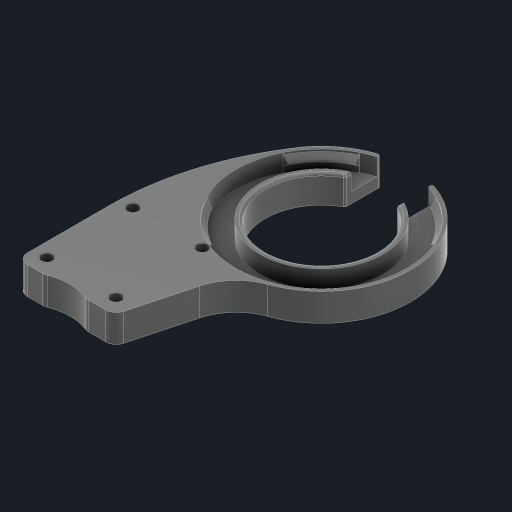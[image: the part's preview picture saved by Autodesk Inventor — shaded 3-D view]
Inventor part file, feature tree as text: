
AUTODESK INVENTOR PART (.ipt)
format: ipt  version: 2023 (Build 270158000, 158)  size: 347,136 bytes
history: native  units: mm
features: extrude x8, fillet x7, sketch x5, draft x2, revolve x1, direct_edit x1, other x1
ambient origin geometry x8: Origin, YZ Plane, XZ Plane, XY Plane, X Axis, Y Axis, Z Axis, Center Point
bodies: Solid1 (feature_tree)
feature tree (25):
  sketch  "Sketch1"  dims[d0=35.5mm d2=49.02mm]
  extrude  "Extrusion1"  Depth=49.02mm
  extrude  "Extrusion2"  Depth=7.0mm TaperAngle=0.0deg
  draft  "FaceDraft1"
  sketch  "Sketch2"  dims[d3=1.2mm d4=7.0mm d5=0.0mm]
  extrude  "Extrusion3"  Depth=2.0mm
  revolve  "Revolution1"  [1 undecoded]
  extrude  "Extrusion4"  Depth=15.0mm TaperAngle=0.0deg
  direct_edit  "Direct Edit3"
  extrude  "Extrusion6"  Depth=15.0mm
  extrude  "Extrusion7"  Depth=3.0mm
  fillet  "Fillet5"  [1 undecoded]
  fillet  "Fillet6"  [1 undecoded]
  sketch  "Sketch6"  dims[d24=3.0mm d25=6.0mm d26=0.0mm d29=3.1mm d30=3.0mm d31=45.0deg d32=90.0deg d33=23.1mm d34=90.0deg d35=0.0mm d36=0.0mm d40=14.9mm d49=-0.127mm d51=3.0mm d52=0.0mm d53=22.0mm d54=22.0mm d55=10.0mm d56=0.0mm d57=0.8mm d58=0.5mm d59=45.0mm d60=8.0mm d62=48.0mm d63=3.0mm d64=0.0mm d65=0.7mm d66=3.2mm d67=24.5mm d68=3.2mm d69=24.9mm d76=0.0mm d78=10.0mm d79=0.0mm d80=30.0mm d81=10.0mm d82=15.0mm d83=75.0mm d84=3.0mm d85=15.0deg d86=15.0mm]
  extrude  "Extrusion8"  Depth=15.0mm
  fillet  "Fillet7"  [1 undecoded]
  extrude  "Extrusion9"  TaperAngle=0.0deg  [1 undecoded]
  fillet  "Fillet12"  Radius=14.9mm
  fillet  "Fillet13"  [1 undecoded]
  draft  "FaceDraft4"
  fillet  "Fillet14"  Radius=3.0mm
  fillet  "Fillet15"  Radius=22.0mm
  sketch  "Sketch3"  dims[d6=2.0mm d7=0.0mm d8=0.401426mm]
  sketch  "Sketch5"  dims[d22=1.6mm d23=14.9mm]
  other  "Size1"
note: 6 required parameter values undecoded (feature->parameter linkage not recoverable at this tier; creation-order binding heuristic only, values carry confidence <= 0.55)